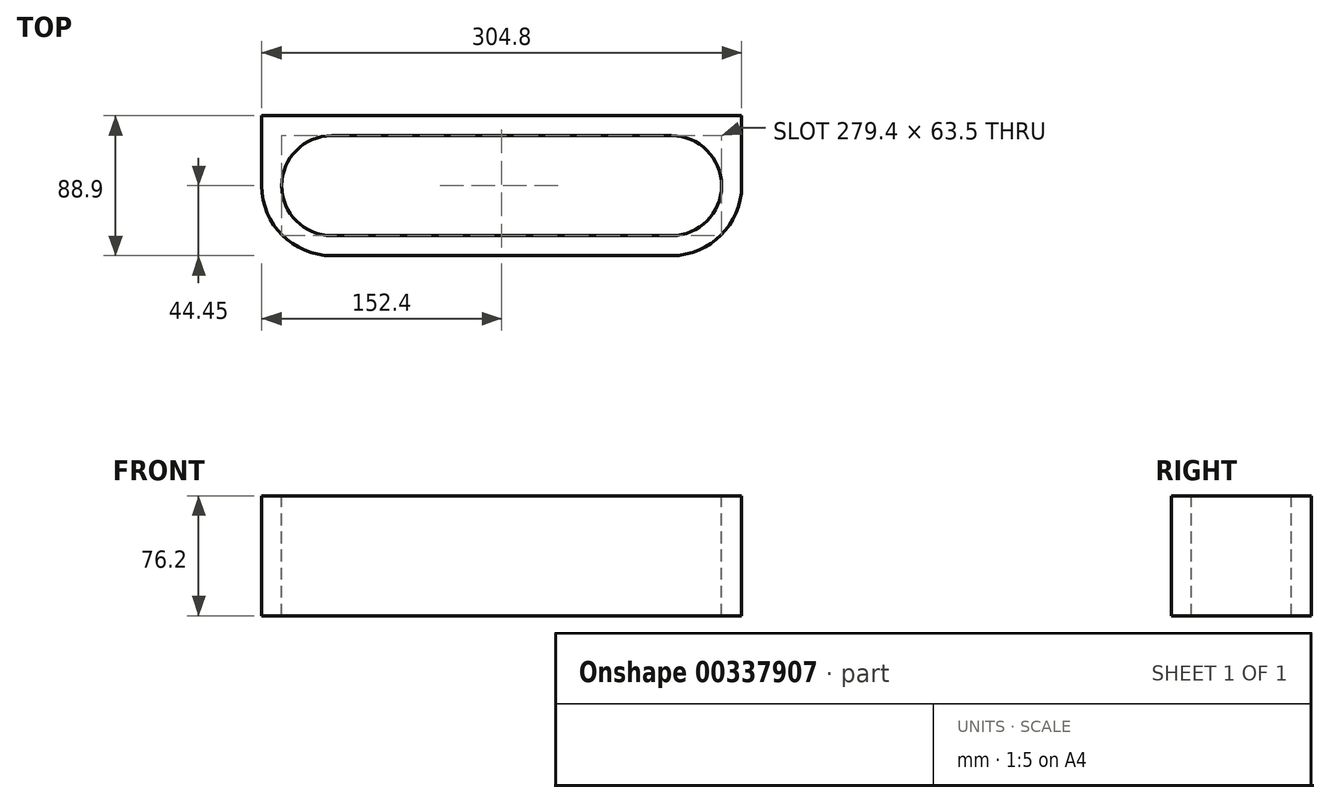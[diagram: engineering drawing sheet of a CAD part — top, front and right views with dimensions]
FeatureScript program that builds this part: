
annotation { "Feature Type Name" : "Feature", "Feature Type Description" : "" }
export const myFeature = defineFeature(function(context is Context, id is Id, definition is map)
    precondition{}
    {
        {
            var Q0;
            Q0=qCreatedBy(makeId("Top.planeOp"),FACE);
            var sketch = newSketch(context, id + "F0", { "sketchPlane" : qUnion([Q0])});
            skLineSegment(sketch, "E0", {"start": v(0, -88.9) * mm, "end": v(152.4, -88.9) * mm});
            skLineSegment(sketch, "E1", {"start": v(152.4, -88.9) * mm, "end": v(152.4, 0) * mm});
            skLineSegment(sketch, "E2", {"start": v(152.4, 0) * mm, "end": v(0, 0) * mm});
            skLineSegment(sketch, "E3", {"start": v(0, 0) * mm, "end": v(-152.4, 0) * mm});
            skLineSegment(sketch, "E4", {"start": v(-152.4, 0) * mm, "end": v(-152.4, -88.9) * mm});
            skLineSegment(sketch, "E5", {"start": v(-152.4, -88.9) * mm, "end": v(0, -88.9) * mm});
            skSolve(sketch);
        }
        {
            var Q0;
            Q0=makeQuery(id+"F0.imprint","IMPRINT",FACE,{"disambiguationData":[TD([[makeQuery(id+"F0.imprint","IMPRINT",EDGE,{"derivedFrom":sQuery(id+"F0.wireOp",EDGE,"E0")}),1.0]])]});
            extrude(context, id + "F1", {"entities" : qUnion([Q0]), "depth" : 76.2 * mm});
        }
        {
            var Q0;
            Q0=makeQuery(id+"F1.opExtrude","CAP_FACE",FACE,{"disambiguationData":[OSD([sQuery(id+"F0.wireOp",EDGE,"E0"),sQuery(id+"F0.wireOp",EDGE,"E1"),sQuery(id+"F0.wireOp",EDGE,"E2"),sQuery(id+"F0.wireOp",EDGE,"E3"),sQuery(id+"F0.wireOp",EDGE,"E4"),sQuery(id+"F0.wireOp",EDGE,"E5")])],"isStart":false});
            var sketch = newSketch(context, id + "F2", { "sketchPlane" : qUnion([Q0])});
            skLineSegment(sketch, "E6", {"start": v(152.4, -88.9) * mm, "end": v(107.95, -88.9) * mm});
            skLineSegment(sketch, "E7", {"start": v(152.4, 0) * mm, "end": v(107.95, 0) * mm});
            skLineSegment(sketch, "E8", {"start": v(-152.4, -88.9) * mm, "end": v(-107.95, -88.9) * mm});
            skLineSegment(sketch, "E9", {"start": v(-152.4, 0) * mm, "end": v(-107.95, 0) * mm});
            skLineSegment(sketch, "E10", {"start": v(107.95, -88.9) * mm, "end": v(107.95, -76.2) * mm});
            skLineSegment(sketch, "E11", {"start": v(-107.95, -88.9) * mm, "end": v(-107.95, -76.2) * mm});
            skArc(sketch, "E12", {"start": v(-152.4, -44.45) * mm, "mid": v(-139.38, -75.88) * mm, "end": v(-107.95, -88.9) * mm});
            skArc(sketch, "E13", {"start": v(152.4, -44.45) * mm, "mid": v(139.38, -75.88) * mm, "end": v(107.95, -88.9) * mm});
            skArc(sketch, "E14", {"start": v(107.95, 0) * mm, "mid": v(139.38, -13.02) * mm, "end": v(152.4, -44.45) * mm});
            skLineSegment(sketch, "E15", {"start": v(0, -12.7) * mm, "end": v(107.95, -12.7) * mm});
            skLineSegment(sketch, "E16", {"start": v(0, -12.7) * mm, "end": v(-107.95, -12.7) * mm});
            skLineSegment(sketch, "E17", {"start": v(0, -76.2) * mm, "end": v(107.95, -76.2) * mm});
            skLineSegment(sketch, "E18", {"start": v(0, -76.2) * mm, "end": v(-107.95, -76.2) * mm});
            skArc(sketch, "E19", {"start": v(107.95, -76.2) * mm, "mid": v(139.7, -44.45) * mm, "end": v(107.95, -12.7) * mm});
            skArc(sketch, "E20", {"start": v(-107.95, -12.7) * mm, "mid": v(-139.7, -44.45) * mm, "end": v(-107.95, -76.2) * mm});
            skLineSegment(sketch, "E21.trimOffspring", {"start": v(107.95, -12.7) * mm, "end": v(107.95, 0) * mm});
            skLineSegment(sketch, "E22.trimOffspring", {"start": v(-107.95, -12.7) * mm, "end": v(-107.95, 0) * mm});
            skSolve(sketch);
        }
        {
            var Q0;
            {var subQ0=sQuery(id+"F2.wireOp",EDGE,"E8");Q0=makeQuery(id+"F2.imprint","IMPRINT",FACE,{"disambiguationData":[TD([[makeQuery(id+"F2.imprint","IMPRINT",EDGE,{"derivedFrom":subQ0}),1.0]])]});}
            extrude(context, id + "F3", {"entities" : qUnion([Q0]), "operationType" : NewBodyOperationType.REMOVE, "oppositeDirection" : true, "depth" : 127 * mm});
        }
        {
            var Q0;
            {var subQ0=sQuery(id+"F2.wireOp",EDGE,"E9");Q0=makeQuery(id+"F2.imprint","IMPRINT",FACE,{"disambiguationData":[TD([[makeQuery(id+"F2.imprint","IMPRINT",EDGE,{"derivedFrom":subQ0}),1.0]])]});}
            extrude(context, id + "F4", {"entities" : qUnion([Q0]), "operationType" : NewBodyOperationType.REMOVE, "oppositeDirection" : true, "depth" : 127 * mm});
        }
        {
            var Q0;
            {var subQ0=sQuery(id+"F2.wireOp",EDGE,"E7");Q0=makeQuery(id+"F2.imprint","IMPRINT",FACE,{"disambiguationData":[TD([[makeQuery(id+"F2.imprint","IMPRINT",EDGE,{"derivedFrom":subQ0}),1.0]])]});}
            extrude(context, id + "F5", {"entities" : qUnion([Q0]), "operationType" : NewBodyOperationType.REMOVE, "oppositeDirection" : true, "depth" : 127 * mm});
        }
        {
            var Q0;
            {var subQ0=sQuery(id+"F2.wireOp",EDGE,"E6");Q0=makeQuery(id+"F2.imprint","IMPRINT",FACE,{"disambiguationData":[TD([[makeQuery(id+"F2.imprint","IMPRINT",EDGE,{"derivedFrom":subQ0}),1.0]])]});}
            extrude(context, id + "F6", {"entities" : qUnion([Q0]), "operationType" : NewBodyOperationType.REMOVE, "oppositeDirection" : true, "depth" : 127 * mm});
        }
        {
            var Q0;
            {var subQ0=sQuery(id+"F2.wireOp",EDGE,"E7");Q0=makeQuery(id+"F2.imprint","IMPRINT",FACE,{"disambiguationData":[TD([[makeQuery(id+"F2.imprint","IMPRINT",EDGE,{"derivedFrom":subQ0}),1.0]])]});}
            extrude(context, id + "F7", {"entities" : qUnion([Q0]), "operationType" : NewBodyOperationType.ADD, "oppositeDirection" : true, "depth" : 76.2 * mm});
        }
        {
            var Q0;
            {var subQ0=sQuery(id+"F2.wireOp",EDGE,"E9");Q0=makeQuery(id+"F2.imprint","IMPRINT",FACE,{"disambiguationData":[TD([[makeQuery(id+"F2.imprint","IMPRINT",EDGE,{"derivedFrom":subQ0}),1.0]])]});}
            extrude(context, id + "F8", {"entities" : qUnion([Q0]), "operationType" : NewBodyOperationType.ADD, "oppositeDirection" : true, "depth" : 76.2 * mm});
        }
        {
            var Q0;
            Q0=makeQuery(id+"F2.imprint","IMPRINT",FACE,{"disambiguationData":[TD([[makeQuery(id+"F2.imprint","IMPRINT",EDGE,{"derivedFrom":sQuery(id+"F2.wireOp",EDGE,"E15")}),-1.0]])]});
            extrude(context, id + "F9", {"entities" : qUnion([Q0]), "operationType" : NewBodyOperationType.REMOVE, "oppositeDirection" : true, "depth" : 76.2 * mm});
        }
        {
            var Q0;
            Q0=makeQuery(id+"F2.imprint","IMPRINT",FACE,{"disambiguationData":[TD([[makeQuery(id+"F2.imprint","IMPRINT",EDGE,{"derivedFrom":sQuery(id+"F2.wireOp",EDGE,"E15")}),-1.0]])]});
            extrude(context, id + "F10", {"entities" : qUnion([Q0]), "operationType" : NewBodyOperationType.REMOVE, "oppositeDirection" : true, "depth" : 76.2 * mm});
        }
    });
